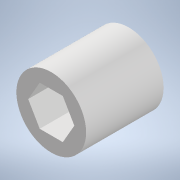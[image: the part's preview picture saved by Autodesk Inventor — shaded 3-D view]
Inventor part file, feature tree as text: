
AUTODESK INVENTOR PART (.ipt)
format: ipt  version: 2020.3 (Build 243373000, 373)  size: 117,248 bytes
history: native  units: mm
features: extrude x3, sketch x3, projected_geometry x1
ambient origin geometry x8: Origin, YZ Plane, XZ Plane, XY Plane, X Axis, Y Axis, Z Axis, Center Point
bodies: Solid1 (feature_tree)
feature tree (7):
  extrude  "Extrusion1"  Depth=25.0mm TaperAngle=0.0deg
  extrude  "Extrusion2"  Depth=13.3mm TaperAngle=0.0deg
  extrude  "Extrusion3"  [1 undecoded]
  sketch  "Sketch1"  dims[d0=22.5mm d1=25.0mm d2=0.0mm]
  sketch  "Sketch2"  dims[d3=13.3mm d4=30.0mm d5=0.0mm]
  sketch  "Sketch3"  dims[d6=10.0mm d7=0.0mm]
  projected_geometry  "Projected Loop1"
note: 1 required parameter value undecoded (feature->parameter linkage not recoverable at this tier; creation-order binding heuristic only, values carry confidence <= 0.55)
